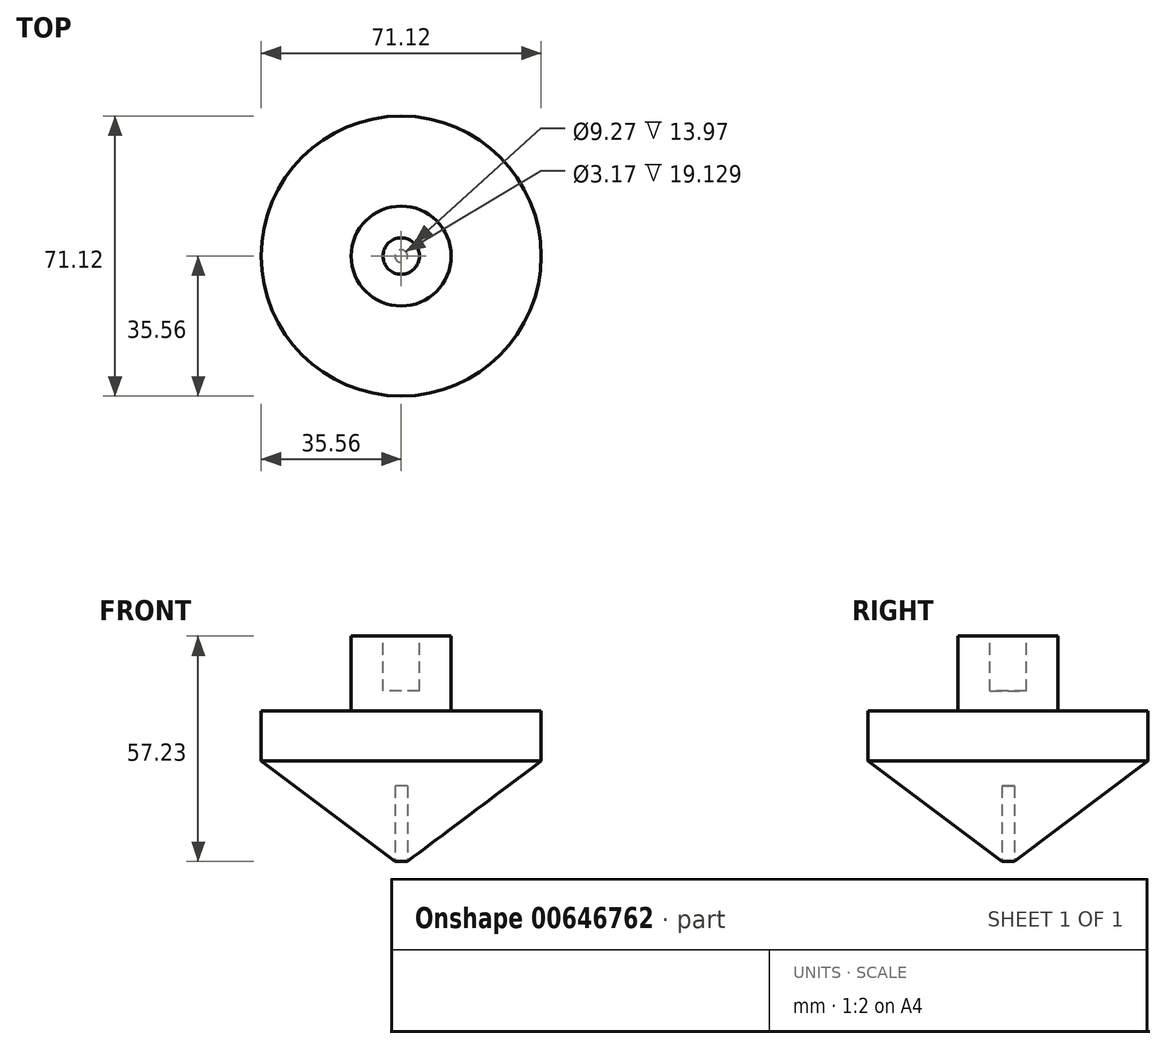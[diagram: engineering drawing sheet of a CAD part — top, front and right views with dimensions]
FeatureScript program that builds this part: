
annotation { "Feature Type Name" : "Feature", "Feature Type Description" : "" }
export const myFeature = defineFeature(function(context is Context, id is Id, definition is map)
    precondition{}
    {
        {
            var Q0;
            Q0=qCreatedBy(makeId("Front.planeOp"),FACE);
            var sketch = newSketch(context, id + "F0", { "sketchPlane" : qUnion([Q0])});
            skLineSegment(sketch, "E0", {"start": v(0, 0) * mm, "end": v(35.56, 26.67) * mm});
            skLineSegment(sketch, "E1", {"start": v(35.56, 26.67) * mm, "end": v(35.56, 39.37) * mm});
            skLineSegment(sketch, "E2", {"start": v(35.56, 39.37) * mm, "end": v(12.7, 39.37) * mm});
            skLineSegment(sketch, "E3", {"start": v(12.7, 39.37) * mm, "end": v(12.7, 58.42) * mm});
            skLineSegment(sketch, "E4", {"start": v(12.7, 58.42) * mm, "end": v(0, 58.42) * mm});
            skLineSegment(sketch, "E5", {"start": v(0, 58.42) * mm, "end": v(0, 0) * mm});
            skSolve(sketch);
        }
        {
            var Q0;
            Q0 = qSketchRegion(id + "F0", true);
            var Q1;
            Q1=sQuery(id+"F0.wireOp",EDGE,"E5");
            revolve(context, id + "F1", {"entities" : qUnion([Q0]), "axis" : qUnion([Q1]), "revolveType" : RevolveType.FULL});
        }
        {
            var Q0;
            Q0=makeQuery(id+"F1.opRevolve","SWEPT_FACE",FACE,{"disambiguationData":[OSD([sQuery(id+"F0.wireOp",EDGE,"E4")])]});
            var sketch = newSketch(context, id + "F2", { "sketchPlane" : qUnion([Q0])});
            skCircle(sketch, "E6", {"center": v(0, 0) * mm, "radius": 4.64 * mm});
            skSolve(sketch);
        }
        {
            var Q0;
            Q0 = qSketchRegion(id + "F2", true);
            extrude(context, id + "F3", {"entities" : qUnion([Q0]), "operationType" : NewBodyOperationType.REMOVE, "oppositeDirection" : true, "depth" : 13.97 * mm, "offsetDistance" : 25.4 * mm});
        }
        {
            var Q0;
            Q0=qCreatedBy(makeId("Top.planeOp"),FACE);
            var sketch = newSketch(context, id + "F4", { "sketchPlane" : qUnion([Q0])});
            skCircle(sketch, "E7", {"center": v(0, 0) * mm, "radius": 1.59 * mm});
            skSolve(sketch);
        }
        {
            var Q0;
            Q0 = qSketchRegion(id + "F4", true);
            extrude(context, id + "F5", {"entities" : qUnion([Q0]), "operationType" : NewBodyOperationType.REMOVE, "depth" : 20.32 * mm, "offsetDistance" : 25.4 * mm});
        }
    });
